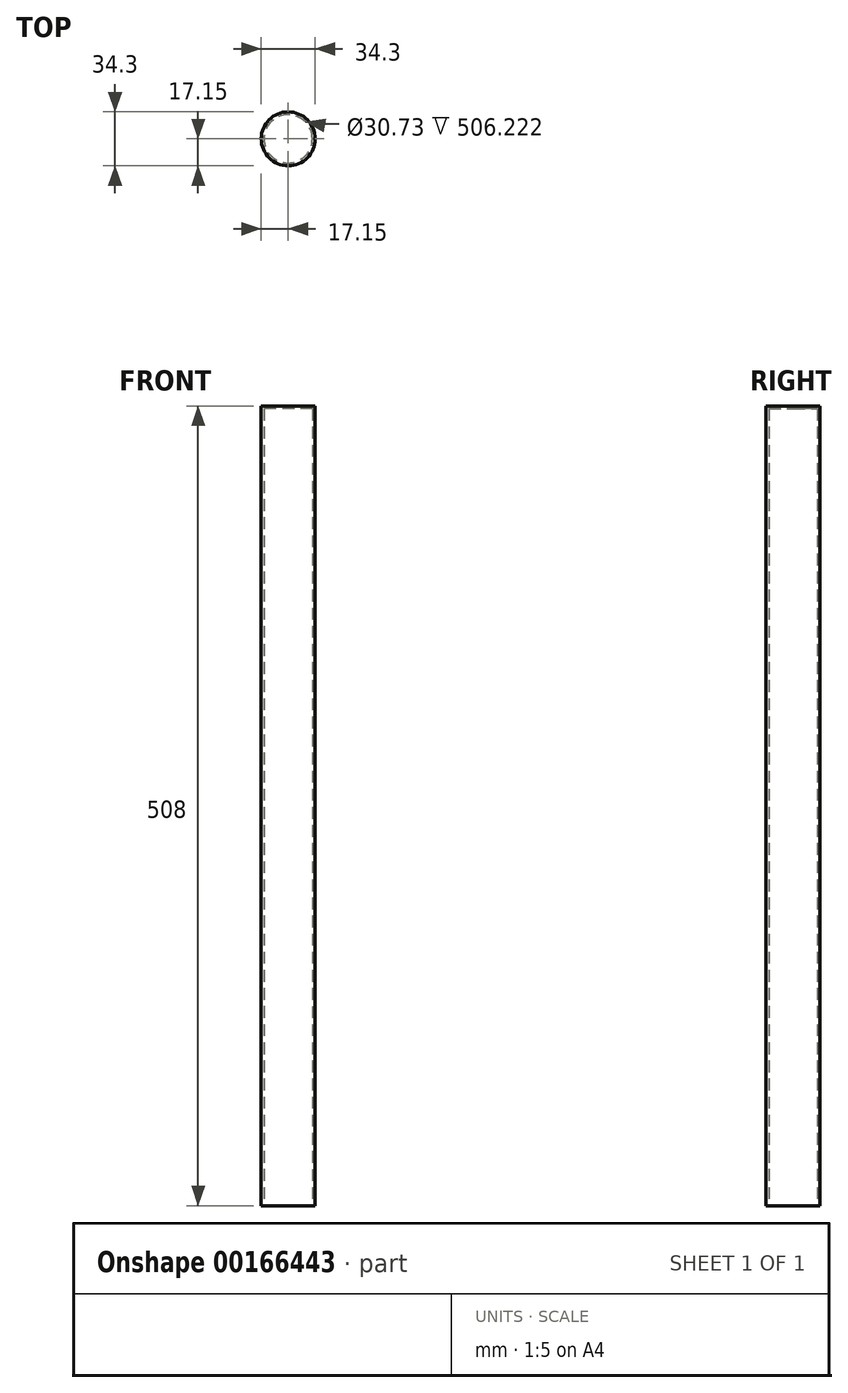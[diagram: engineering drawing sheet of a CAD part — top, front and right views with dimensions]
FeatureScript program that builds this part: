
annotation { "Feature Type Name" : "Feature", "Feature Type Description" : "" }
export const myFeature = defineFeature(function(context is Context, id is Id, definition is map)
    precondition{}
    {
        {
            var Q0;
            Q0=qCreatedBy(makeId("Top.planeOp"),FACE);
            var sketch = newSketch(context, id + "F0", { "sketchPlane" : qUnion([Q0])});
            skCircle(sketch, "E0", {"center": v(0, 0) * mm, "radius": 17.15 * mm});
            skSolve(sketch);
        }
        {
            var Q0;
            Q0=makeQuery(id+"F0.imprint","IMPRINT",FACE,{"disambiguationData":[TD([[makeQuery(id+"F0.imprint","IMPRINT",EDGE,{"derivedFrom":sQuery(id+"F0.wireOp",EDGE,"E0")}),1.0]])]});
            extrude(context, id + "F1", {"entities" : qUnion([Q0]), "endBound" : BoundingType.SYMMETRIC, "depth" : 508 * mm});
        }
        {
            var Q0;
            Q0=makeQuery(id+"F1.opExtrude","CAP_FACE",FACE,{"disambiguationData":[OSD([sQuery(id+"F0.wireOp",EDGE,"E0")])],"isStart":true});
            shell(context, id + "F2", {"entities" : qUnion([Q0]), "thickness" : 1.78 * mm});
        }
    });
